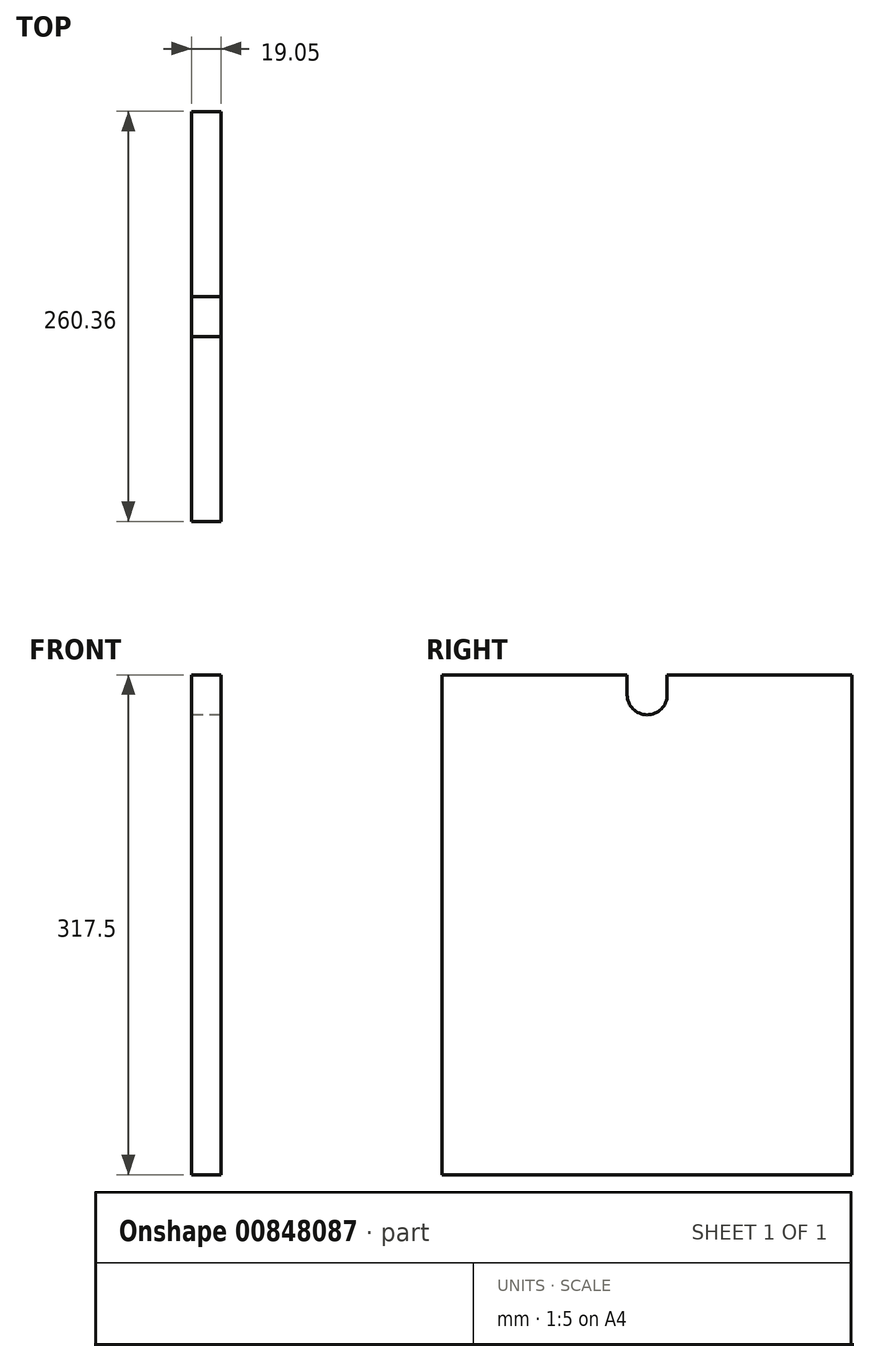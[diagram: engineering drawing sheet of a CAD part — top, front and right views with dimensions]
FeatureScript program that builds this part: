
annotation { "Feature Type Name" : "Feature", "Feature Type Description" : "" }
export const myFeature = defineFeature(function(context is Context, id is Id, definition is map)
    precondition{}
    {
        {
            var Q0;
            Q0=qCreatedBy(makeId("Right.planeOp"),FACE);
            var sketch = newSketch(context, id + "F0", { "sketchPlane" : qUnion([Q0])});
            skLineSegment(sketch, "E0.bottom", {"start": v(130.17, 158.75) * mm, "end": v(-130.18, 158.75) * mm});
            skLineSegment(sketch, "E0.top", {"start": v(130.17, -158.75) * mm, "end": v(-130.18, -158.75) * mm});
            skLineSegment(sketch, "E0.left", {"start": v(130.17, 158.75) * mm, "end": v(130.17, -158.75) * mm});
            skLineSegment(sketch, "E0.right", {"start": v(-130.18, 158.75) * mm, "end": v(-130.18, -158.75) * mm});
            skPoint(sketch, "E0.middle", {"position": v(0, 0) * mm});
            skLineSegment(sketch, "E1", {"start": v(0, 158.75) * mm, "end": v(0, 146.05) * mm});
            skCircle(sketch, "E2", {"center": v(0, 146.05) * mm, "radius": 12.7 * mm});
            skLineSegment(sketch, "E3", {"start": v(0, 146.05) * mm, "end": v(-12.7, 146.05) * mm});
            skLineSegment(sketch, "E4", {"start": v(-12.7, 146.05) * mm, "end": v(-12.7, 158.75) * mm});
            skLineSegment(sketch, "E5", {"start": v(0, 146.05) * mm, "end": v(12.7, 146.05) * mm});
            skLineSegment(sketch, "E6", {"start": v(12.7, 146.05) * mm, "end": v(12.7, 158.75) * mm});
            skSolve(sketch);
        }
        {
            var Q0;
            Q0=makeQuery(id+"F0.imprint","IMPRINT",FACE,{"disambiguationData":[TD([[makeQuery(id+"F0.imprint","IMPRINT",EDGE,{"derivedFrom":sQuery(id+"F0.wireOp",EDGE,"E0.bottom")}),1.0]])]});
            extrude(context, id + "F1", {"entities" : qUnion([Q0]), "depth" : 19.05 * mm, "offsetDistance" : 25.4 * mm});
        }
    });
